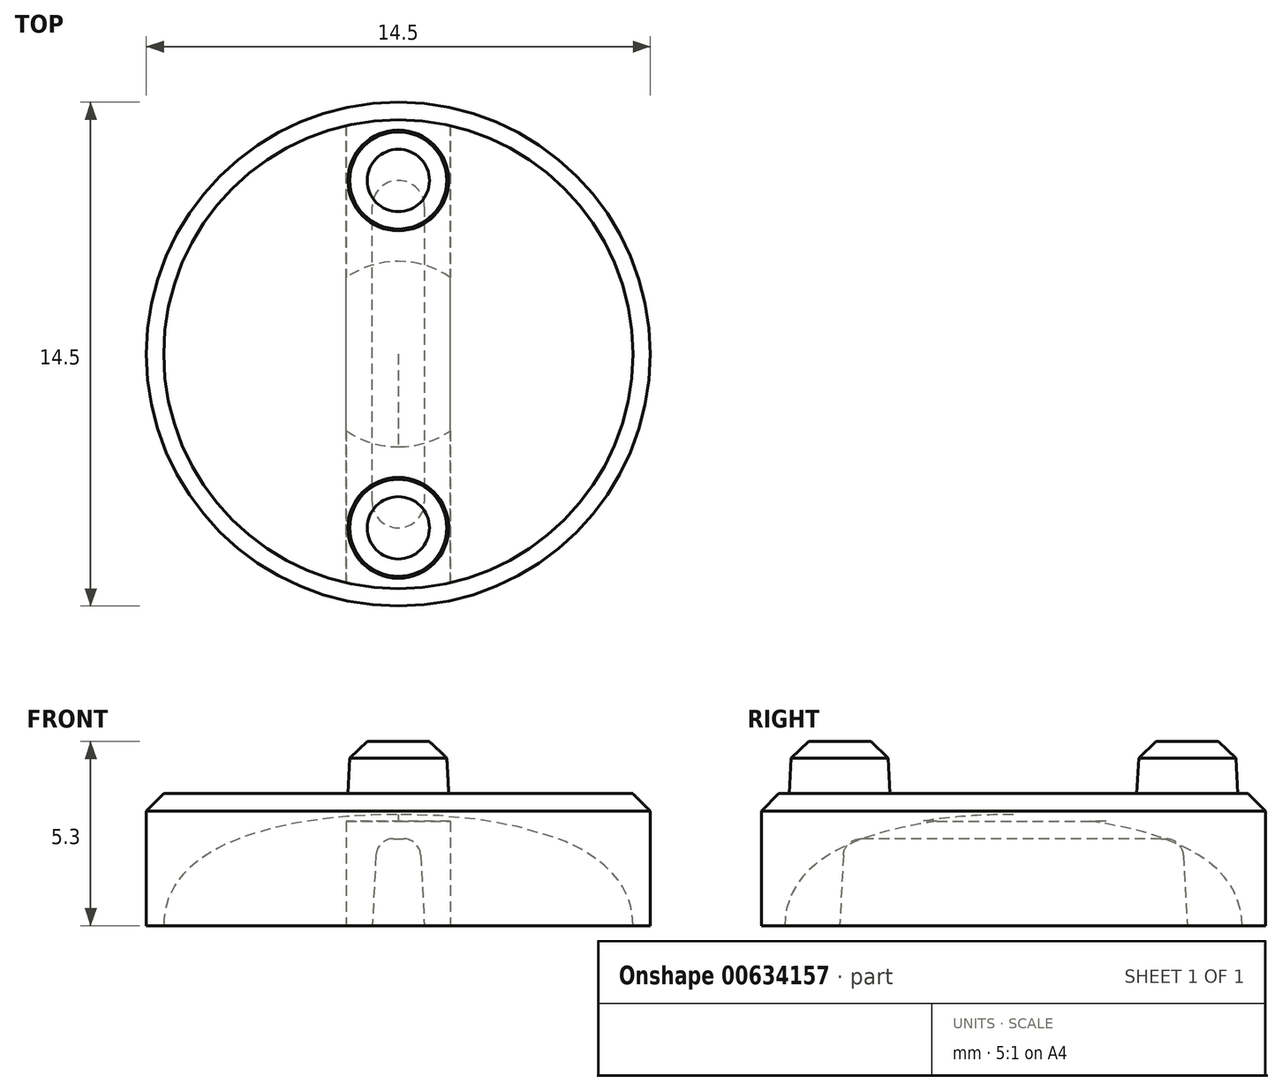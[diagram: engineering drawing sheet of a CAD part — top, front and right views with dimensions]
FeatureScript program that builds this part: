
annotation { "Feature Type Name" : "Feature", "Feature Type Description" : "" }
export const myFeature = defineFeature(function(context is Context, id is Id, definition is map)
    precondition{}
    {
        {
            var Q0;
            Q0=qCreatedBy(makeId("Top.planeOp"),FACE);
            var sketch = newSketch(context, id + "F0", { "sketchPlane" : qUnion([Q0])});
            skCircle(sketch, "E0", {"center": v(0, 0) * mm, "radius": 7.25 * mm});
            skLineSegment(sketch, "E1", {"start": v(0, -14.83) * mm, "end": v(0, 18.75) * mm, "construction": true});
            skSolve(sketch);
        }
        {
            var Q0;
            Q0 = qSketchRegion(id + "F0", true);
            extrude(context, id + "F1", {"entities" : qUnion([Q0]), "depth" : 3.8 * mm, "offsetDistance" : 25 * mm});
        }
        {
            var Q0;
            Q0=makeQuery(id+"F1.opExtrude","CAP_FACE",FACE,{"disambiguationData":[OSD([sQuery(id+"F0.wireOp",EDGE,"E0")])],"isStart":false});
            var sketch = newSketch(context, id + "F2", { "sketchPlane" : qUnion([Q0])});
            skLineSegment(sketch, "E2.0", {"start": v(0, -14.83) * mm, "end": v(0, 18.75) * mm, "construction": true});
            skCircle(sketch, "E3", {"center": v(0, 5) * mm, "radius": 1.45 * mm});
            skCircle(sketch, "E4", {"center": v(0, -5) * mm, "radius": 1.45 * mm});
            skSolve(sketch);
        }
        {
            var Q0;
            Q0 = qSketchRegion(id + "F2", true);
            extrude(context, id + "F3", {"entities" : qUnion([Q0]), "operationType" : NewBodyOperationType.ADD, "depth" : 1.5 * mm, "offsetDistance" : 25 * mm, "hasDraft" : true, "draftAngle" : 3 * degree, "draftPullDirection" : true});
        }
        {
            var Q0;
            Q0=makeQuery(id+"F3.opExtrude","CAP_EDGE",EDGE,{"disambiguationData":[OSD([sQuery(id+"F2.wireOp",EDGE,"E3")])],"isStart":false});
            var Q1;
            Q1=makeQuery(id+"F3.opExtrude","CAP_EDGE",EDGE,{"disambiguationData":[OSD([sQuery(id+"F2.wireOp",EDGE,"E4")])],"isStart":false});
            chamfer(context, id + "F4", {"entities" : qUnion([Q0, Q1]), "width" : 0.5 * mm, "tangentPropagation" : true});
        }
        {
            var Q0;
            Q0=qCreatedBy(makeId("Right.planeOp"),FACE);
            var sketch = newSketch(context, id + "F5", { "sketchPlane" : qUnion([Q0])});
            skLineSegment(sketch, "E5.0", {"start": v(-6.75, 0) * mm, "end": v(0, 0) * mm});
            skLineSegment(sketch, "E6", {"start": v(0, 0) * mm, "end": v(0, 3.2) * mm});
            skFitSpline(sketch, "E7", {"points": [v(0, 3.2) * mm, v(-6.75, 0) * mm], "startDerivative": vector(-9, 0) * mm, "endDerivative": vector(0, -7.5) * mm});
            skPoint(sketch, "E8.orphan", {"position": v(7.25, 0) * mm});
            skLineSegment(sketch, "E9", {"start": v(0, -3.04) * mm, "end": v(0, 8.95) * mm, "construction": true});
            skPoint(sketch, "E10.orphan", {"position": v(-7.25, 0) * mm});
            skSolve(sketch);
        }
        {
            var Q0;
            Q0 = qSketchRegion(id + "F5", true);
            var Q1;
            Q1=sQuery(id+"F5.wireOp",EDGE,"E9");
            revolve(context, id + "F6", {"operationType" : NewBodyOperationType.REMOVE, "entities" : qUnion([Q0]), "axis" : qUnion([Q1]), "revolveType" : RevolveType.FULL, "oppositeDirection" : true});
        }
        {
            var Q0;
            Q0=makeQuery(id+"F0.imprint","IMPRINT",FACE,{"disambiguationData":[TD([[makeQuery(id+"F0.imprint","IMPRINT",EDGE,{"derivedFrom":sQuery(id+"F0.wireOp",EDGE,"E0")}),1.0]])]});
            var sketch = newSketch(context, id + "F7", { "sketchPlane" : qUnion([Q0])});
            skLineSegment(sketch, "E11.0", {"start": v(0, -14.83) * mm, "end": v(0, 18.75) * mm, "construction": true});
            skArc(sketch, "E12.0", {"start": v(-1.5, -6.58) * mm, "mid": v(0, -6.75) * mm, "end": v(1.5, -6.58) * mm});
            skLineSegment(sketch, "E13.0", {"start": v(1.5, -6.58) * mm, "end": v(1.5, 6.58) * mm});
            skLineSegment(sketch, "E14.0", {"start": v(-1.5, -6.58) * mm, "end": v(-1.5, 6.58) * mm});
            skArc(sketch, "E15.trimOffspring", {"start": v(1.5, 6.58) * mm, "mid": v(0, 6.75) * mm, "end": v(-1.5, 6.58) * mm});
            skSolve(sketch);
        }
        {
            var Q0;
            Q0 = qSketchRegion(id + "F7", true);
            extrude(context, id + "F8", {"entities" : qUnion([Q0]), "operationType" : NewBodyOperationType.ADD, "depth" : 3 * mm, "offsetDistance" : 25 * mm});
        }
        {
            var Q0;
            Q0=makeQuery(id+"F8.boolean.opBoolean","MERGE",FACE,{"derivedFrom":[makeQuery(id+"F1.opExtrude","CAP_FACE",FACE,{"disambiguationData":[OSD([sQuery(id+"F0.wireOp",EDGE,"E0")])],"isStart":true}),makeQuery(id+"F8.opExtrude","CAP_FACE",FACE,{"disambiguationData":[OSD([sQuery(id+"F7.wireOp",EDGE,"E12.0"),sQuery(id+"F7.wireOp",EDGE,"E13.0"),sQuery(id+"F7.wireOp",EDGE,"E14.0"),sQuery(id+"F7.wireOp",EDGE,"E15.trimOffspring")])],"isStart":true})]});
            var sketch = newSketch(context, id + "F9", { "sketchPlane" : qUnion([Q0])});
            skLineSegment(sketch, "E16", {"start": v(0, 4.25) * mm, "end": v(0, -4.25) * mm, "construction": true});
            skArc(sketch, "E17.0.startCap", {"start": v(-0.75, 4.25) * mm, "mid": v(0, 5) * mm, "end": v(0.75, 4.25) * mm});
            skArc(sketch, "E17.0.endCap", {"start": v(0.75, -4.25) * mm, "mid": v(0, -5) * mm, "end": v(-0.75, -4.25) * mm});
            skLineSegment(sketch, "E17.0.left", {"start": v(0.75, 4.25) * mm, "end": v(0.75, -4.25) * mm});
            skLineSegment(sketch, "E17.0.right", {"start": v(-0.75, 4.25) * mm, "end": v(-0.75, -4.25) * mm});
            skSolve(sketch);
        }
        {
            var Q0;
            Q0 = qSketchRegion(id + "F9", true);
            extrude(context, id + "F10", {"entities" : qUnion([Q0]), "operationType" : NewBodyOperationType.REMOVE, "oppositeDirection" : true, "depth" : 2.5 * mm, "offsetDistance" : 25 * mm, "hasDraft" : true, "draftAngle" : 3 * degree, "draftPullDirection" : true});
        }
        {
            var Q0;
            Q0=makeQuery(id+"F10.boolean.opBoolean","COPY",FACE,{"derivedFrom":makeQuery(id+"F10.opExtrude","CAP_FACE",FACE,{"disambiguationData":[OSD([sQuery(id+"F9.wireOp",EDGE,"E17.0.startCap"),sQuery(id+"F9.wireOp",EDGE,"E17.0.endCap"),sQuery(id+"F9.wireOp",EDGE,"E17.0.left"),sQuery(id+"F9.wireOp",EDGE,"E17.0.right")])],"isStart":false})});
            fillet(context, id + "F11", {"entities" : qUnion([Q0]), "radius" : 0.5 * mm, "tangentPropagation" : true, "allowEdgeOverflow" : false});
        }
        {
            var Q0;
            Q0=makeQuery(id+"F1.opExtrude","CAP_EDGE",EDGE,{"disambiguationData":[OSD([sQuery(id+"F0.wireOp",EDGE,"E0")])],"isStart":false});
            chamfer(context, id + "F12", {"entities" : qUnion([Q0]), "width" : 0.5 * mm, "tangentPropagation" : true});
        }
    });
